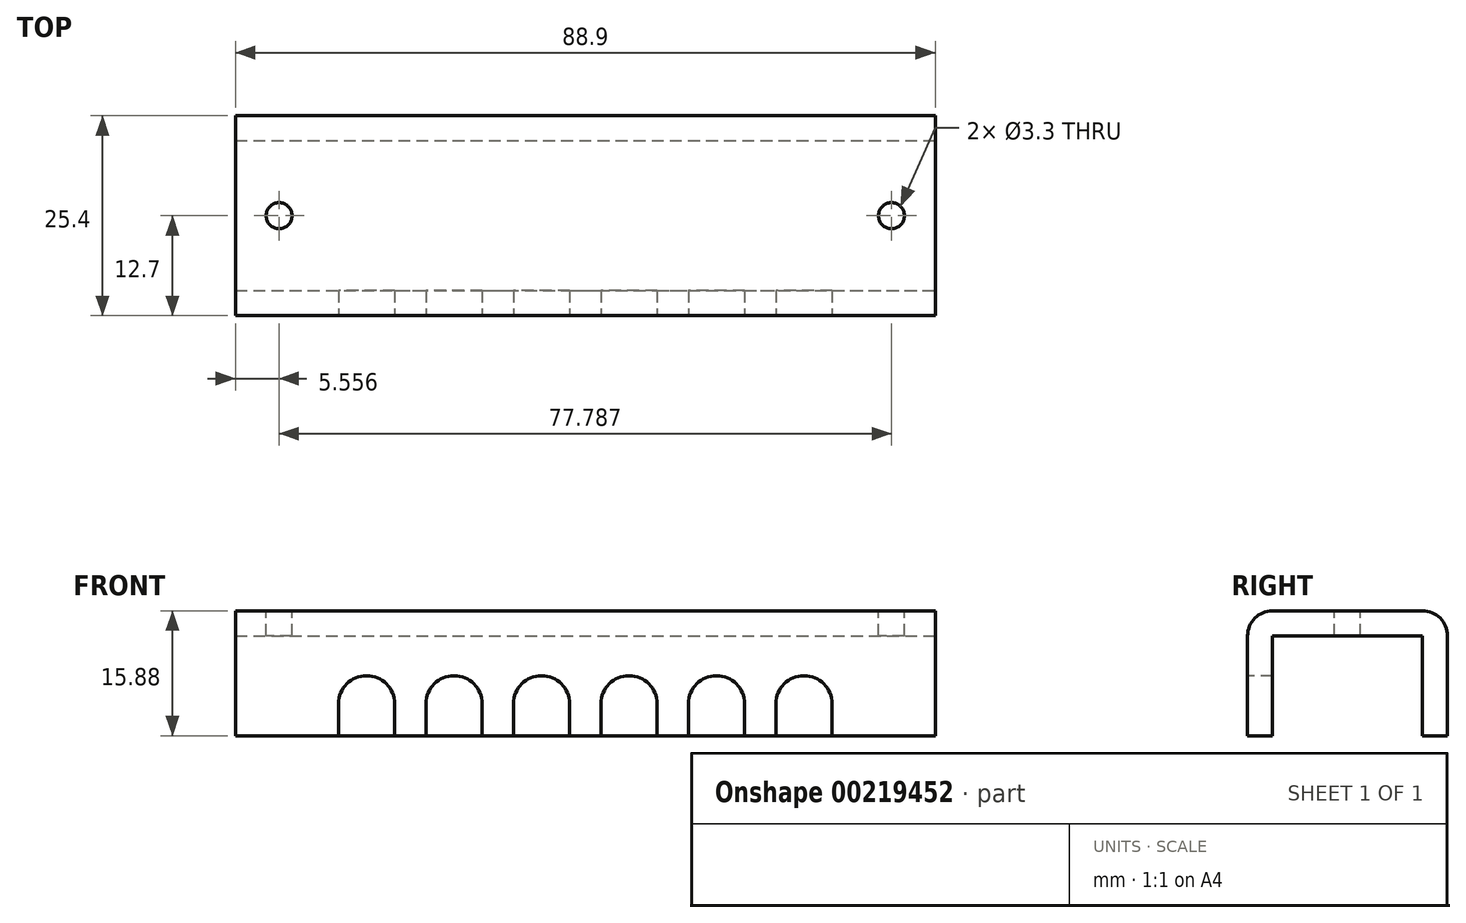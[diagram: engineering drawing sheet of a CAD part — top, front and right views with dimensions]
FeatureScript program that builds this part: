
annotation { "Feature Type Name" : "Feature", "Feature Type Description" : "" }
export const myFeature = defineFeature(function(context is Context, id is Id, definition is map)
    precondition{}
    {
        {
            var Q0;
            Q0=qCreatedBy(makeId("Top.planeOp"),FACE);
            var sketch = newSketch(context, id + "F0", { "sketchPlane" : qUnion([Q0])});
            skLineSegment(sketch, "E0.bottom", {"start": v(44.45, -12.7) * mm, "end": v(-44.45, -12.7) * mm});
            skLineSegment(sketch, "E0.top", {"start": v(44.45, 12.7) * mm, "end": v(-44.45, 12.7) * mm});
            skLineSegment(sketch, "E0.left", {"start": v(44.45, -12.7) * mm, "end": v(44.45, 12.7) * mm});
            skLineSegment(sketch, "E0.right", {"start": v(-44.45, -12.7) * mm, "end": v(-44.45, 12.7) * mm});
            skPoint(sketch, "E0.middle", {"position": v(0, 0) * mm});
            skSolve(sketch);
        }
        {
            var Q0;
            Q0=makeQuery(id+"F0.imprint","IMPRINT",FACE,{"disambiguationData":[TD([[makeQuery(id+"F0.imprint","IMPRINT",EDGE,{"derivedFrom":sQuery(id+"F0.wireOp",EDGE,"E0.bottom")}),-1.0]])]});
            extrude(context, id + "F1", {"entities" : qUnion([Q0]), "depth" : 3.17 * mm});
        }
        {
            var Q0;
            Q0=makeQuery(id+"F1.opExtrude","CAP_FACE",FACE,{"disambiguationData":[OSD([sQuery(id+"F0.wireOp",EDGE,"E0.bottom"),sQuery(id+"F0.wireOp",EDGE,"E0.top"),sQuery(id+"F0.wireOp",EDGE,"E0.left"),sQuery(id+"F0.wireOp",EDGE,"E0.right")])],"isStart":true});
            var sketch = newSketch(context, id + "F2", { "sketchPlane" : qUnion([Q0])});
            skLineSegment(sketch, "E1.bottom", {"start": v(-44.45, 12.7) * mm, "end": v(44.45, 12.7) * mm});
            skLineSegment(sketch, "E1.top", {"start": v(-44.45, 9.53) * mm, "end": v(44.45, 9.53) * mm});
            skLineSegment(sketch, "E1.left", {"start": v(-44.45, 12.7) * mm, "end": v(-44.45, 9.53) * mm});
            skLineSegment(sketch, "E1.right", {"start": v(44.45, 12.7) * mm, "end": v(44.45, 9.53) * mm});
            skLineSegment(sketch, "E2.bottom", {"start": v(-44.45, -12.7) * mm, "end": v(44.45, -12.7) * mm});
            skLineSegment(sketch, "E2.top", {"start": v(-44.45, -9.52) * mm, "end": v(44.45, -9.52) * mm});
            skLineSegment(sketch, "E2.left", {"start": v(-44.45, -12.7) * mm, "end": v(-44.45, -9.52) * mm});
            skLineSegment(sketch, "E2.right", {"start": v(44.45, -12.7) * mm, "end": v(44.45, -9.52) * mm});
            skSolve(sketch);
        }
        {
            var Q0;
            Q0=qSketchRegion(id+"F2",true);
            extrude(context, id + "F3", {"entities" : qUnion([Q0]), "operationType" : NewBodyOperationType.ADD, "depth" : 12.7 * mm});
        }
        {
            var Q0;
            Q0=makeQuery(id+"F1.opExtrude","CAP_FACE",FACE,{"disambiguationData":[OSD([sQuery(id+"F0.wireOp",EDGE,"E0.bottom"),sQuery(id+"F0.wireOp",EDGE,"E0.top"),sQuery(id+"F0.wireOp",EDGE,"E0.left"),sQuery(id+"F0.wireOp",EDGE,"E0.right")])],"isStart":false});
            var sketch = newSketch(context, id + "F4", { "sketchPlane" : qUnion([Q0])});
            skPoint(sketch, "E3", {"position": v(-38.9, 0) * mm});
            skPoint(sketch, "E4", {"position": v(38.9, 0) * mm});
            skSolve(sketch);
        }
        {
            var Q0;
            Q0=sQuery(id+"F4.wireOp",VERTEX,"E3");
            var Q1;
            Q1=sQuery(id+"F4.wireOp",VERTEX,"E4");
            var Q2;
            Q2=makeQuery(id+"F1.opExtrude","SWEPT_BODY",BODY,{"disambiguationData":[OSD([sQuery(id+"F0.wireOp",EDGE,"E0.bottom"),sQuery(id+"F0.wireOp",EDGE,"E0.top"),sQuery(id+"F0.wireOp",EDGE,"E0.left"),sQuery(id+"F0.wireOp",EDGE,"E0.right")])]});
            hole(context, id + "F5", {"style" : HoleStyle.SIMPLE, "endStyle" : HoleEndStyle.THROUGH, "standardTappedOrClearance" : lookupTablePath({ "standard" : "ISO", "fit" : "Normal", "size" : "M3", "type" : "Clearance" }), "standardBlindInLast" : lookupTablePath({ "fit" : "Standard", "standard" : "ISO", "size" : "M3", "type" : "Clearance" }), "holeDiameter" : 3.3 * mm, "locations" : qUnion([Q0, Q1]), "scope" : qUnion([Q2]), "isTappedThrough" : true});
        }
        {
            var Q0;
            Q0=makeQuery(id+"F3.boolean.opBoolean","MERGE",FACE,{"derivedFrom":[makeQuery(id+"F1.opExtrude","SWEPT_FACE",FACE,{"disambiguationData":[OSD([sQuery(id+"F0.wireOp",EDGE,"E0.bottom")])]}),makeQuery(id+"F3.opExtrude","SWEPT_FACE",FACE,{"disambiguationData":[OSD([sQuery(id+"F2.wireOp",EDGE,"E1.bottom")])]})]});
            var sketch = newSketch(context, id + "F6", { "sketchPlane" : qUnion([Q0])});
            skCircle(sketch, "E5", {"center": v(-27.78, -8.64) * mm, "radius": 3.57 * mm});
            skCircle(sketch, "E6", {"center": v(-16.67, -8.64) * mm, "radius": 3.57 * mm});
            skCircle(sketch, "E7", {"center": v(-5.56, -8.64) * mm, "radius": 3.57 * mm});
            skCircle(sketch, "E8", {"center": v(5.56, -8.64) * mm, "radius": 3.57 * mm});
            skCircle(sketch, "E9", {"center": v(16.67, -8.64) * mm, "radius": 3.57 * mm});
            skCircle(sketch, "E10", {"center": v(27.78, -8.64) * mm, "radius": 3.57 * mm});
            skLineSegment(sketch, "E11.bottom", {"start": v(-31.35, -12.7) * mm, "end": v(-24.2, -12.7) * mm});
            skLineSegment(sketch, "E11.top", {"start": v(-31.35, -8.64) * mm, "end": v(-24.2, -8.64) * mm});
            skLineSegment(sketch, "E11.left", {"start": v(-31.35, -12.7) * mm, "end": v(-31.35, -8.64) * mm});
            skLineSegment(sketch, "E11.right", {"start": v(-24.2, -12.7) * mm, "end": v(-24.2, -8.64) * mm});
            skLineSegment(sketch, "E12.bottom", {"start": v(-20.24, -8.64) * mm, "end": v(-13.1, -8.64) * mm});
            skLineSegment(sketch, "E12.top", {"start": v(-20.24, -12.7) * mm, "end": v(-13.1, -12.7) * mm});
            skLineSegment(sketch, "E12.left", {"start": v(-20.24, -8.64) * mm, "end": v(-20.24, -12.7) * mm});
            skLineSegment(sketch, "E12.right", {"start": v(-13.1, -8.64) * mm, "end": v(-13.1, -12.7) * mm});
            skLineSegment(sketch, "E13.bottom", {"start": v(-9.13, -8.64) * mm, "end": v(-1.98, -8.64) * mm});
            skLineSegment(sketch, "E13.top", {"start": v(-9.13, -12.7) * mm, "end": v(-1.98, -12.7) * mm});
            skLineSegment(sketch, "E13.left", {"start": v(-9.13, -8.64) * mm, "end": v(-9.13, -12.7) * mm});
            skLineSegment(sketch, "E13.right", {"start": v(-1.98, -8.64) * mm, "end": v(-1.98, -12.7) * mm});
            skLineSegment(sketch, "E14.bottom", {"start": v(1.98, -8.64) * mm, "end": v(9.13, -8.64) * mm});
            skLineSegment(sketch, "E14.top", {"start": v(1.98, -12.7) * mm, "end": v(9.13, -12.7) * mm});
            skLineSegment(sketch, "E14.left", {"start": v(1.98, -8.64) * mm, "end": v(1.98, -12.7) * mm});
            skLineSegment(sketch, "E14.right", {"start": v(9.13, -8.64) * mm, "end": v(9.13, -12.7) * mm});
            skLineSegment(sketch, "E15.bottom", {"start": v(13.1, -8.64) * mm, "end": v(20.24, -8.64) * mm});
            skLineSegment(sketch, "E15.top", {"start": v(13.1, -12.7) * mm, "end": v(20.24, -12.7) * mm});
            skLineSegment(sketch, "E15.left", {"start": v(13.1, -8.64) * mm, "end": v(13.1, -12.7) * mm});
            skLineSegment(sketch, "E15.right", {"start": v(20.24, -8.64) * mm, "end": v(20.24, -12.7) * mm});
            skLineSegment(sketch, "E16.bottom", {"start": v(24.2, -8.64) * mm, "end": v(31.35, -8.64) * mm});
            skLineSegment(sketch, "E16.top", {"start": v(24.2, -12.7) * mm, "end": v(31.35, -12.7) * mm});
            skLineSegment(sketch, "E16.left", {"start": v(24.2, -8.64) * mm, "end": v(24.2, -12.7) * mm});
            skLineSegment(sketch, "E16.right", {"start": v(31.35, -8.64) * mm, "end": v(31.35, -12.7) * mm});
            skSolve(sketch);
        }
        {
            var Q0;
            Q0=qSketchRegion(id+"F6",true);
            extrude(context, id + "F7", {"entities" : qUnion([Q0]), "operationType" : NewBodyOperationType.REMOVE, "oppositeDirection" : true, "depth" : 3.17 * mm});
        }
        {
            var Q0;
            Q0=makeQuery(id+"F1.opExtrude","CAP_EDGE",EDGE,{"disambiguationData":[OSD([sQuery(id+"F0.wireOp",EDGE,"E0.bottom")])],"isStart":false});
            var Q1;
            Q1=makeQuery(id+"F1.opExtrude","CAP_EDGE",EDGE,{"disambiguationData":[OSD([sQuery(id+"F0.wireOp",EDGE,"E0.top")])],"isStart":false});
            fillet(context, id + "F8", {"entities" : qUnion([Q0, Q1]), "radius" : 3.17 * mm, "tangentPropagation" : true});
        }
    });
